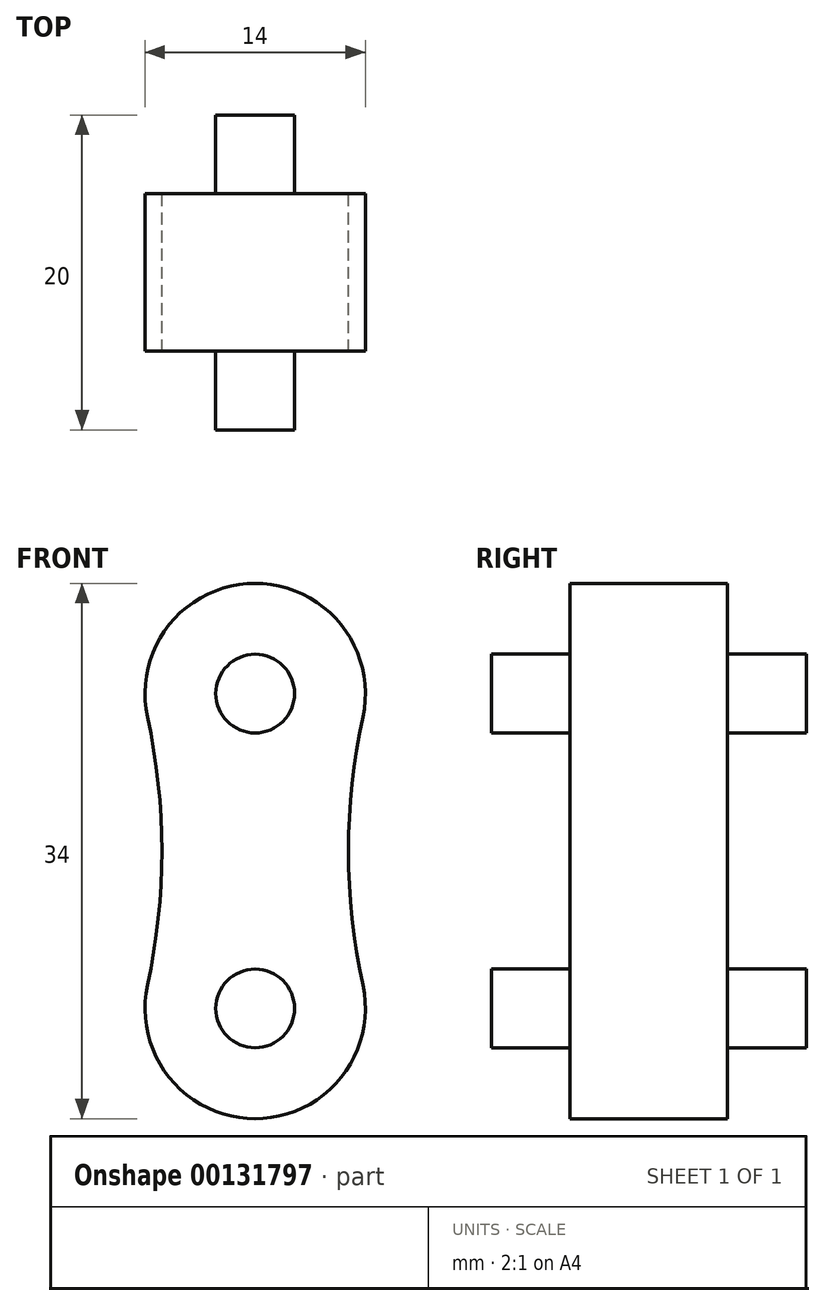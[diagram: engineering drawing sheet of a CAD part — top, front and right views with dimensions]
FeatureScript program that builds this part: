
annotation { "Feature Type Name" : "Feature", "Feature Type Description" : "" }
export const myFeature = defineFeature(function(context is Context, id is Id, definition is map)
    precondition{}
    {
        {
            var Q0;
            Q0=qCreatedBy(makeId("Front.planeOp"),FACE);
            var sketch = newSketch(context, id + "F0", { "sketchPlane" : qUnion([Q0])});
            skArc(sketch, "E0", {"start": v(-6.84, -8.51) * mm, "mid": v(0, -17) * mm, "end": v(6.84, -8.51) * mm});
            skArc(sketch, "E1", {"start": v(6.84, 8.51) * mm, "mid": v(0, 17) * mm, "end": v(-6.84, 8.51) * mm});
            skArc(sketch, "E2", {"start": v(-6.84, -8.51) * mm, "mid": v(-5.92, 0) * mm, "end": v(-6.84, 8.51) * mm});
            skArc(sketch, "E3", {"start": v(6.84, 8.51) * mm, "mid": v(5.92, 0) * mm, "end": v(6.84, -8.51) * mm});
            skSolve(sketch);
        }
        {
            var Q0;
            Q0 = qSketchRegion(id + "F0", true);
            extrude(context, id + "F1", {"entities" : qUnion([Q0]), "depth" : 10 * mm});
        }
        {
            var Q0;
            Q0=makeQuery(id+"F1.opExtrude","CAP_FACE",FACE,{"disambiguationData":[OSD([sQuery(id+"F0.wireOp",EDGE,"E0"),sQuery(id+"F0.wireOp",EDGE,"E1"),sQuery(id+"F0.wireOp",EDGE,"E2"),sQuery(id+"F0.wireOp",EDGE,"E3")])],"isStart":true});
            var sketch = newSketch(context, id + "F2", { "sketchPlane" : qUnion([Q0])});
            skCircle(sketch, "E4", {"center": v(0, 10) * mm, "radius": 2.5 * mm});
            skCircle(sketch, "E5", {"center": v(0, -10) * mm, "radius": 2.5 * mm});
            skSolve(sketch);
        }
        {
            var Q0;
            Q0=makeQuery(id+"F2.imprint","IMPRINT",FACE,{"disambiguationData":[TD([[makeQuery(id+"F2.imprint","IMPRINT",EDGE,{"derivedFrom":sQuery(id+"F2.wireOp",EDGE,"E4")}),1.0]])]});
            var Q1;
            Q1=makeQuery(id+"F2.imprint","IMPRINT",FACE,{"disambiguationData":[TD([[makeQuery(id+"F2.imprint","IMPRINT",EDGE,{"derivedFrom":sQuery(id+"F2.wireOp",EDGE,"E5")}),1.0]])]});
            extrude(context, id + "F3", {"entities" : qUnion([Q0, Q1]), "operationType" : NewBodyOperationType.ADD, "depth" : 5 * mm, "hasSecondDirection" : true, "secondDirectionOppositeDirection" : true, "secondDirectionDepth" : 15 * mm});
        }
    });
